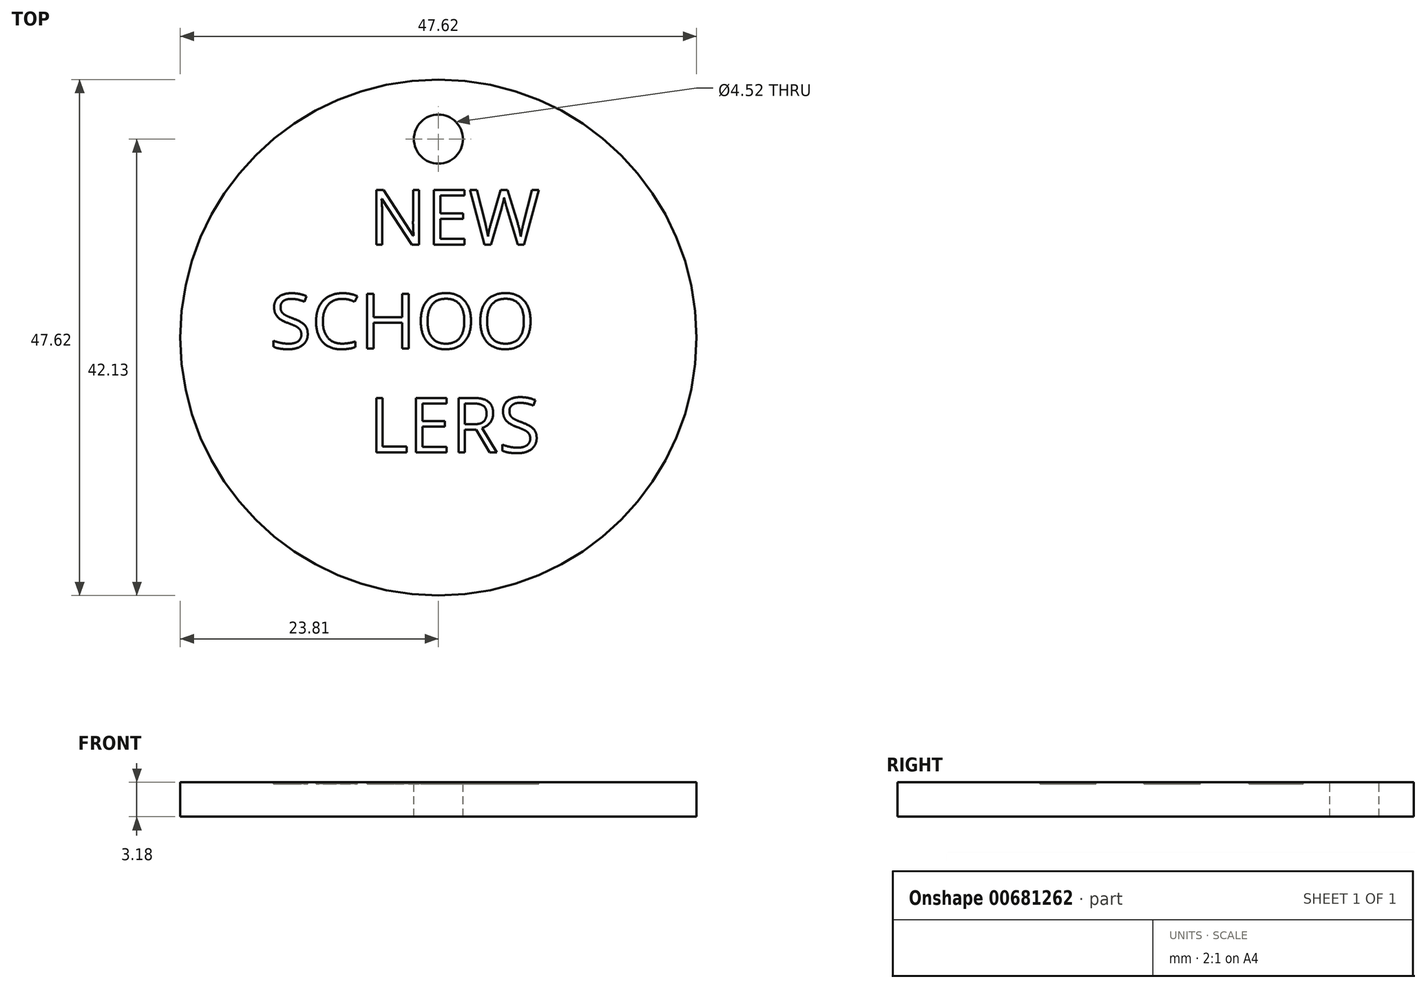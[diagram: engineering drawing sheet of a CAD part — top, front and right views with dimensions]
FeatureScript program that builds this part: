
annotation { "Feature Type Name" : "Feature", "Feature Type Description" : "" }
export const myFeature = defineFeature(function(context is Context, id is Id, definition is map)
    precondition{}
    {
        {
            var Q0;
            Q0=qCreatedBy(makeId("Top.planeOp"),FACE);
            var sketch = newSketch(context, id + "F0", { "sketchPlane" : qUnion([Q0])});
            skCircle(sketch, "E0", {"center": v(0, 0) * mm, "radius": 23.81 * mm});
            skSolve(sketch);
        }
        {
            var Q0;
            Q0=makeQuery(id+"F0.imprint","IMPRINT",FACE,{"disambiguationData":[TD([[makeQuery(id+"F0.imprint","IMPRINT",EDGE,{"derivedFrom":sQuery(id+"F0.wireOp",EDGE,"E0")}),1.0]])]});
            extrude(context, id + "F1", {"entities" : qUnion([Q0]), "depth" : 3.17 * mm, "offsetDistance" : 25.4 * mm});
        }
        {
            var Q0;
            Q0=makeQuery(id+"F1.opExtrude","CAP_FACE",FACE,{"disambiguationData":[OSD([sQuery(id+"F0.wireOp",EDGE,"E0")])],"isStart":false});
            var sketch = newSketch(context, id + "F2", { "sketchPlane" : qUnion([Q0])});
            skText(sketch, "E1", { "text": "     NEW\nSCHOO\n     LERS", "fontName": "OpenSans-Regular.ttf"});
            const initialGuessF2  = {"E1": [-0.01559, 0.00858, 1, 0, 0.00508]};
            skSetInitialGuess(sketch, initialGuessF2);
            skSolve(sketch);
        }
        {
            var Q0;
            Q0 = qSketchRegion(id + "F2", true);
            extrude(context, id + "F3", {"entities" : qUnion([Q0]), "operationType" : NewBodyOperationType.REMOVE, "oppositeDirection" : true, "depth" : 0.15 * mm, "offsetDistance" : 25.4 * mm});
        }
        {
            var Q0;
            {var subQ0=sQuery(id+"F0.wireOp",EDGE,"E0");Q0=makeQuery(id+"F3.boolean.opBoolean","SPLIT",FACE,{"disambiguationData":[TD([makeQuery(id+"F1.opExtrude","SWEPT_FACE",FACE,{"disambiguationData":[OSD([subQ0])]})])],"derivedFrom":makeQuery(id+"F1.opExtrude","CAP_FACE",FACE,{"disambiguationData":[OSD([subQ0])],"isStart":false})});}
            var sketch = newSketch(context, id + "F4", { "sketchPlane" : qUnion([Q0])});
            skCircle(sketch, "E2", {"center": v(0, 18.32) * mm, "radius": 2.26 * mm});
            skSolve(sketch);
        }
        {
            var Q0;
            Q0=makeQuery(id+"F4.imprint","IMPRINT",FACE,{"disambiguationData":[TD([[makeQuery(id+"F4.imprint","IMPRINT",EDGE,{"derivedFrom":sQuery(id+"F4.wireOp",EDGE,"E2")}),1.0]])]});
            extrude(context, id + "F5", {"entities" : qUnion([Q0]), "operationType" : NewBodyOperationType.REMOVE, "endBound" : BoundingType.THROUGH_ALL, "oppositeDirection" : true, "depth" : 25.4 * mm, "offsetDistance" : 25.4 * mm});
        }
    });
